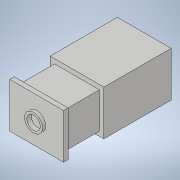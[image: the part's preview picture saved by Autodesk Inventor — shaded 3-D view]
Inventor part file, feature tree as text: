
AUTODESK INVENTOR PART (.ipt)
format: ipt  version: 2020 (Build 240168000, 168)  size: 141,312 bytes
history: native  units: mm
features: extrude x6, sketch x6, other x1
ambient origin geometry x8: Origin, YZ Plane, XZ Plane, XY Plane, X Axis, Y Axis, Z Axis, Center Point
bodies: Body1 (feature_tree)
feature tree (13):
  other  "Твердое тело1"
  extrude  "Выдавливание1"  Depth=12.0mm
  extrude  "Выдавливание2"  Depth=10.0mm
  extrude  "Выдавливание4"  Depth=1.0mm TaperAngle=0.0deg
  extrude  "Выдавливание5"  Depth=4.0mm
  extrude  "Выдавливание9"  Depth=0.7mm TaperAngle=0.0deg
  extrude  "Выдавливание6"  Depth=8.0mm TaperAngle=0.0deg
  sketch  "Эскиз2"
  sketch  "Эскиз3"
  sketch  "Эскиз5"
  sketch  "Эскиз6"
  sketch  "Эскиз8"
  sketch  "Эскиз11"
